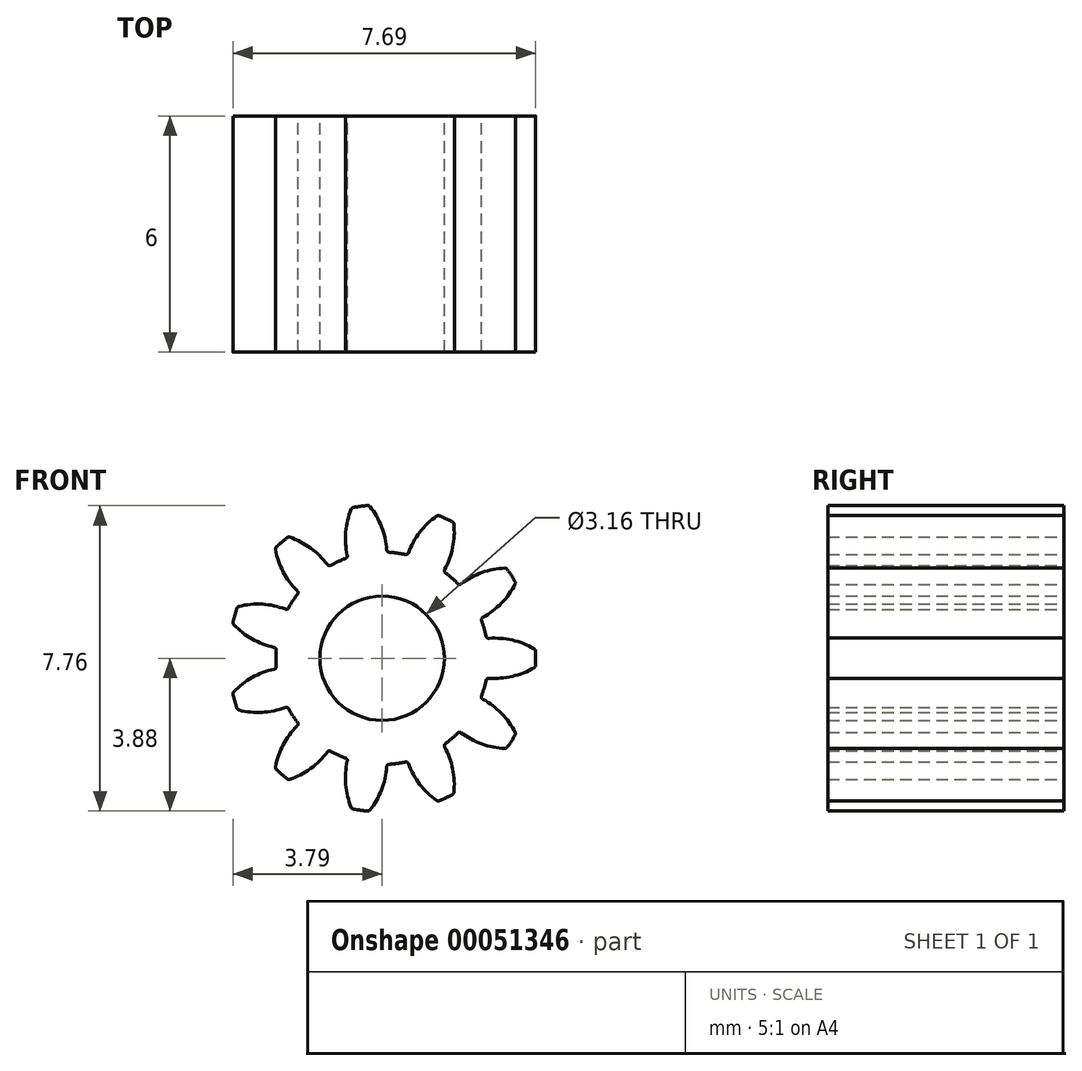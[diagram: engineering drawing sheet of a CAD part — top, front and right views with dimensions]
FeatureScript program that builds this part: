
annotation { "Feature Type Name" : "Feature", "Feature Type Description" : "" }
export const myFeature = defineFeature(function(context is Context, id is Id, definition is map)
    precondition{}
    {
        {
            var Q0;
            Q0=qCreatedBy(makeId("Front.planeOp"),FACE);
            var sketch = newSketch(context, id + "F0", { "sketchPlane" : qUnion([Q0])});
            skLineSegment(sketch, "E0", {"start": v(0, 0) * mm, "end": v(0, 6) * mm, "construction": true});
            skCircle(sketch, "E1", {"center": v(0, 0) * mm, "radius": 2.7 * mm, "construction": true});
            skCircle(sketch, "E2", {"center": v(0, 0) * mm, "radius": 3.3 * mm, "construction": true});
            skCircle(sketch, "E3", {"center": v(0, 0) * mm, "radius": 3.9 * mm, "construction": true});
            skLineSegment(sketch, "E4", {"start": v(0, 0) * mm, "end": v(-0.9, 6.31) * mm, "construction": true});
            skLineSegment(sketch, "E5", {"start": v(0, 3.3) * mm, "end": v(-3.91, 3.3) * mm, "construction": true});
            skLineSegment(sketch, "E6", {"start": v(0, 3.3) * mm, "end": v(-4.13, 1.8) * mm, "construction": true});
            skCircle(sketch, "E7", {"center": v(0, 3.3) * mm, "radius": 1.98 * mm, "construction": true});
            skCircle(sketch, "E8", {"center": v(-1.86, 2.62) * mm, "radius": 1.98 * mm, "construction": true});
            skArc(sketch, "E9", {"start": v(0.11, 2.76) * mm, "mid": v(-0.01, 3.34) * mm, "end": v(-0.31, 3.86) * mm});
            skArc(sketch, "E10.MirrorCS", {"start": v(-0.89, 2.61) * mm, "mid": v(-0.93, 3.2) * mm, "end": v(-0.79, 3.79) * mm});
            skArc(sketch, "E11", {"start": v(-0.37, 3.88) * mm, "mid": v(-0.56, 3.86) * mm, "end": v(-0.74, 3.83) * mm});
            skArc(sketch, "E12", {"start": v(0.18, 2.7) * mm, "mid": v(0.38, -2.67) * mm, "end": v(-0.93, 2.54) * mm});
            skPoint(sketch, "E13.visualSharp", {"position": v(0.12, 2.7) * mm});
            skArc(sketch, "E13.filletArc", {"start": v(0.11, 2.76) * mm, "mid": v(0.13, 2.71) * mm, "end": v(0.18, 2.7) * mm});
            skPoint(sketch, "E14.visualSharp", {"position": v(-0.34, 3.89) * mm});
            skArc(sketch, "E14.filletArc", {"start": v(-0.31, 3.86) * mm, "mid": v(-0.34, 3.88) * mm, "end": v(-0.37, 3.88) * mm});
            skPoint(sketch, "E15.visualSharp", {"position": v(-0.77, 3.82) * mm});
            skArc(sketch, "E15.filletArc", {"start": v(-0.74, 3.83) * mm, "mid": v(-0.77, 3.82) * mm, "end": v(-0.79, 3.79) * mm});
            skPoint(sketch, "E16.visualSharp", {"position": v(-0.87, 2.55) * mm});
            skArc(sketch, "E16.filletArc", {"start": v(-0.93, 2.54) * mm, "mid": v(-0.9, 2.57) * mm, "end": v(-0.89, 2.61) * mm});
            skArc(sketch, "E17.1.0", {"start": v(-2.15, 1.63) * mm, "mid": v(-2.14, 1.68) * mm, "end": v(-2.16, 1.72) * mm});
            skArc(sketch, "E17.1.1", {"start": v(-2.16, 1.72) * mm, "mid": v(-2.51, 2.2) * mm, "end": v(-2.71, 2.76) * mm});
            skArc(sketch, "E17.1.2", {"start": v(-2.7, 2.82) * mm, "mid": v(-2.7, 2.8) * mm, "end": v(-2.71, 2.76) * mm});
            skArc(sketch, "E17.1.3", {"start": v(-2.41, 3.07) * mm, "mid": v(-2.55, 2.95) * mm, "end": v(-2.7, 2.82) * mm});
            skArc(sketch, "E17.1.4", {"start": v(-2.35, 3.08) * mm, "mid": v(-2.38, 3.08) * mm, "end": v(-2.41, 3.07) * mm});
            skArc(sketch, "E17.1.5", {"start": v(-1.4, 2.38) * mm, "mid": v(-1.82, 2.8) * mm, "end": v(-2.35, 3.08) * mm});
            skArc(sketch, "E17.1.6", {"start": v(-1.4, 2.38) * mm, "mid": v(-1.35, 2.36) * mm, "end": v(-1.3, 2.36) * mm});
            skArc(sketch, "E17.2.0", {"start": v(-2.7, 0.2) * mm, "mid": v(-2.7, 0.25) * mm, "end": v(-2.74, 0.28) * mm});
            skArc(sketch, "E17.2.1", {"start": v(-2.74, 0.28) * mm, "mid": v(-3.3, 0.49) * mm, "end": v(-3.77, 0.86) * mm});
            skArc(sketch, "E17.2.2", {"start": v(-3.8, 0.92) * mm, "mid": v(-3.79, 0.89) * mm, "end": v(-3.77, 0.86) * mm});
            skArc(sketch, "E17.2.3", {"start": v(-3.69, 1.28) * mm, "mid": v(-3.74, 1.1) * mm, "end": v(-3.8, 0.92) * mm});
            skArc(sketch, "E17.2.4", {"start": v(-3.64, 1.32) * mm, "mid": v(-3.67, 1.3) * mm, "end": v(-3.69, 1.28) * mm});
            skArc(sketch, "E17.2.5", {"start": v(-2.46, 1.25) * mm, "mid": v(-3.04, 1.37) * mm, "end": v(-3.64, 1.32) * mm});
            skArc(sketch, "E17.2.6", {"start": v(-2.46, 1.25) * mm, "mid": v(-2.41, 1.25) * mm, "end": v(-2.38, 1.28) * mm});
            skArc(sketch, "E17.3.0", {"start": v(-2.38, -1.28) * mm, "mid": v(-2.41, -1.25) * mm, "end": v(-2.46, -1.25) * mm});
            skArc(sketch, "E17.3.1", {"start": v(-2.46, -1.25) * mm, "mid": v(-3.04, -1.37) * mm, "end": v(-3.64, -1.32) * mm});
            skArc(sketch, "E17.3.2", {"start": v(-3.69, -1.28) * mm, "mid": v(-3.67, -1.3) * mm, "end": v(-3.64, -1.32) * mm});
            skArc(sketch, "E17.3.3", {"start": v(-3.8, -0.92) * mm, "mid": v(-3.74, -1.1) * mm, "end": v(-3.69, -1.28) * mm});
            skArc(sketch, "E17.3.4", {"start": v(-3.77, -0.86) * mm, "mid": v(-3.79, -0.89) * mm, "end": v(-3.8, -0.92) * mm});
            skArc(sketch, "E17.3.5", {"start": v(-2.74, -0.28) * mm, "mid": v(-3.3, -0.49) * mm, "end": v(-3.77, -0.86) * mm});
            skArc(sketch, "E17.3.6", {"start": v(-2.74, -0.28) * mm, "mid": v(-2.7, -0.25) * mm, "end": v(-2.7, -0.2) * mm});
            skArc(sketch, "E17.4.0", {"start": v(-1.3, -2.36) * mm, "mid": v(-1.35, -2.36) * mm, "end": v(-1.4, -2.38) * mm});
            skArc(sketch, "E17.4.1", {"start": v(-1.4, -2.38) * mm, "mid": v(-1.82, -2.8) * mm, "end": v(-2.35, -3.08) * mm});
            skArc(sketch, "E17.4.2", {"start": v(-2.41, -3.07) * mm, "mid": v(-2.38, -3.08) * mm, "end": v(-2.35, -3.08) * mm});
            skArc(sketch, "E17.4.3", {"start": v(-2.7, -2.82) * mm, "mid": v(-2.55, -2.95) * mm, "end": v(-2.41, -3.07) * mm});
            skArc(sketch, "E17.4.4", {"start": v(-2.71, -2.76) * mm, "mid": v(-2.7, -2.8) * mm, "end": v(-2.7, -2.82) * mm});
            skArc(sketch, "E17.4.5", {"start": v(-2.16, -1.72) * mm, "mid": v(-2.51, -2.2) * mm, "end": v(-2.71, -2.76) * mm});
            skArc(sketch, "E17.4.6", {"start": v(-2.16, -1.72) * mm, "mid": v(-2.14, -1.68) * mm, "end": v(-2.15, -1.63) * mm});
            skArc(sketch, "E17.5.0", {"start": v(0.18, -2.7) * mm, "mid": v(0.13, -2.71) * mm, "end": v(0.11, -2.76) * mm});
            skArc(sketch, "E17.5.1", {"start": v(0.11, -2.76) * mm, "mid": v(-0.01, -3.34) * mm, "end": v(-0.31, -3.86) * mm});
            skArc(sketch, "E17.5.2", {"start": v(-0.37, -3.88) * mm, "mid": v(-0.34, -3.88) * mm, "end": v(-0.31, -3.86) * mm});
            skArc(sketch, "E17.5.3", {"start": v(-0.74, -3.83) * mm, "mid": v(-0.56, -3.86) * mm, "end": v(-0.37, -3.88) * mm});
            skArc(sketch, "E17.5.4", {"start": v(-0.79, -3.79) * mm, "mid": v(-0.77, -3.82) * mm, "end": v(-0.74, -3.83) * mm});
            skArc(sketch, "E17.5.5", {"start": v(-0.89, -2.61) * mm, "mid": v(-0.93, -3.2) * mm, "end": v(-0.79, -3.79) * mm});
            skArc(sketch, "E17.5.6", {"start": v(-0.89, -2.61) * mm, "mid": v(-0.9, -2.57) * mm, "end": v(-0.93, -2.54) * mm});
            skArc(sketch, "E17.6.0", {"start": v(1.6, -2.17) * mm, "mid": v(1.58, -2.21) * mm, "end": v(1.59, -2.26) * mm});
            skArc(sketch, "E17.6.1", {"start": v(1.59, -2.26) * mm, "mid": v(1.8, -2.82) * mm, "end": v(1.82, -3.41) * mm});
            skArc(sketch, "E17.6.2", {"start": v(1.79, -3.47) * mm, "mid": v(1.81, -3.45) * mm, "end": v(1.82, -3.41) * mm});
            skArc(sketch, "E17.6.3", {"start": v(1.45, -3.62) * mm, "mid": v(1.62, -3.55) * mm, "end": v(1.79, -3.47) * mm});
            skArc(sketch, "E17.6.4", {"start": v(1.39, -3.61) * mm, "mid": v(1.42, -3.62) * mm, "end": v(1.45, -3.62) * mm});
            skArc(sketch, "E17.6.5", {"start": v(0.67, -2.68) * mm, "mid": v(0.96, -3.2) * mm, "end": v(1.39, -3.61) * mm});
            skArc(sketch, "E17.6.6", {"start": v(0.67, -2.68) * mm, "mid": v(0.64, -2.64) * mm, "end": v(0.59, -2.63) * mm});
            skArc(sketch, "E17.7.0", {"start": v(2.52, -0.96) * mm, "mid": v(2.52, -1) * mm, "end": v(2.55, -1.04) * mm});
            skArc(sketch, "E17.7.1", {"start": v(2.55, -1.04) * mm, "mid": v(3.03, -1.4) * mm, "end": v(3.38, -1.89) * mm});
            skArc(sketch, "E17.7.2", {"start": v(3.38, -1.95) * mm, "mid": v(3.39, -1.92) * mm, "end": v(3.38, -1.89) * mm});
            skArc(sketch, "E17.7.3", {"start": v(3.18, -2.26) * mm, "mid": v(3.28, -2.1) * mm, "end": v(3.38, -1.95) * mm});
            skArc(sketch, "E17.7.4", {"start": v(3.12, -2.29) * mm, "mid": v(3.15, -2.28) * mm, "end": v(3.18, -2.26) * mm});
            skArc(sketch, "E17.7.5", {"start": v(2, -1.9) * mm, "mid": v(2.53, -2.18) * mm, "end": v(3.12, -2.29) * mm});
            skArc(sketch, "E17.7.6", {"start": v(2, -1.9) * mm, "mid": v(1.96, -1.88) * mm, "end": v(1.92, -1.9) * mm});
            skArc(sketch, "E17.8.0", {"start": v(2.64, 0.56) * mm, "mid": v(2.67, 0.52) * mm, "end": v(2.71, 0.5) * mm});
            skArc(sketch, "E17.8.1", {"start": v(2.71, 0.5) * mm, "mid": v(3.3, 0.46) * mm, "end": v(3.86, 0.24) * mm});
            skArc(sketch, "E17.8.2", {"start": v(3.9, 0.19) * mm, "mid": v(3.89, 0.22) * mm, "end": v(3.86, 0.24) * mm});
            skArc(sketch, "E17.8.3", {"start": v(3.9, -0.19) * mm, "mid": v(3.9, 0) * mm, "end": v(3.9, 0.19) * mm});
            skArc(sketch, "E17.8.4", {"start": v(3.86, -0.24) * mm, "mid": v(3.89, -0.22) * mm, "end": v(3.9, -0.19) * mm});
            skArc(sketch, "E17.8.5", {"start": v(2.71, -0.5) * mm, "mid": v(3.3, -0.46) * mm, "end": v(3.86, -0.24) * mm});
            skArc(sketch, "E17.8.6", {"start": v(2.71, -0.5) * mm, "mid": v(2.67, -0.52) * mm, "end": v(2.64, -0.56) * mm});
            skArc(sketch, "E17.9.0", {"start": v(1.92, 1.9) * mm, "mid": v(1.96, 1.88) * mm, "end": v(2, 1.9) * mm});
            skArc(sketch, "E17.9.1", {"start": v(2, 1.9) * mm, "mid": v(2.53, 2.18) * mm, "end": v(3.12, 2.29) * mm});
            skArc(sketch, "E17.9.2", {"start": v(3.18, 2.26) * mm, "mid": v(3.15, 2.28) * mm, "end": v(3.12, 2.29) * mm});
            skArc(sketch, "E17.9.3", {"start": v(3.38, 1.95) * mm, "mid": v(3.28, 2.1) * mm, "end": v(3.18, 2.26) * mm});
            skArc(sketch, "E17.9.4", {"start": v(3.38, 1.89) * mm, "mid": v(3.39, 1.92) * mm, "end": v(3.38, 1.95) * mm});
            skArc(sketch, "E17.9.5", {"start": v(2.55, 1.04) * mm, "mid": v(3.03, 1.4) * mm, "end": v(3.38, 1.89) * mm});
            skArc(sketch, "E17.9.6", {"start": v(2.55, 1.04) * mm, "mid": v(2.52, 1) * mm, "end": v(2.52, 0.96) * mm});
            skArc(sketch, "E17.10.0", {"start": v(0.59, 2.63) * mm, "mid": v(0.64, 2.64) * mm, "end": v(0.67, 2.68) * mm});
            skArc(sketch, "E17.10.1", {"start": v(0.67, 2.68) * mm, "mid": v(0.96, 3.2) * mm, "end": v(1.39, 3.61) * mm});
            skArc(sketch, "E17.10.2", {"start": v(1.45, 3.62) * mm, "mid": v(1.42, 3.62) * mm, "end": v(1.39, 3.61) * mm});
            skArc(sketch, "E17.10.3", {"start": v(1.79, 3.47) * mm, "mid": v(1.62, 3.55) * mm, "end": v(1.45, 3.62) * mm});
            skArc(sketch, "E17.10.4", {"start": v(1.82, 3.41) * mm, "mid": v(1.81, 3.45) * mm, "end": v(1.79, 3.47) * mm});
            skArc(sketch, "E17.10.5", {"start": v(1.59, 2.26) * mm, "mid": v(1.8, 2.82) * mm, "end": v(1.82, 3.41) * mm});
            skArc(sketch, "E17.10.6", {"start": v(1.59, 2.26) * mm, "mid": v(1.58, 2.21) * mm, "end": v(1.6, 2.17) * mm});
            skCircle(sketch, "E18", {"center": v(0, 0) * mm, "radius": 1.58 * mm});
            skSolve(sketch);
        }
        {
            var Q0;
            Q0 = qSketchRegion(id + "F0", true);
            extrude(context, id + "F1", {"entities" : qUnion([Q0]), "depth" : 6 * mm, "symmetric" : true});
        }
    });
